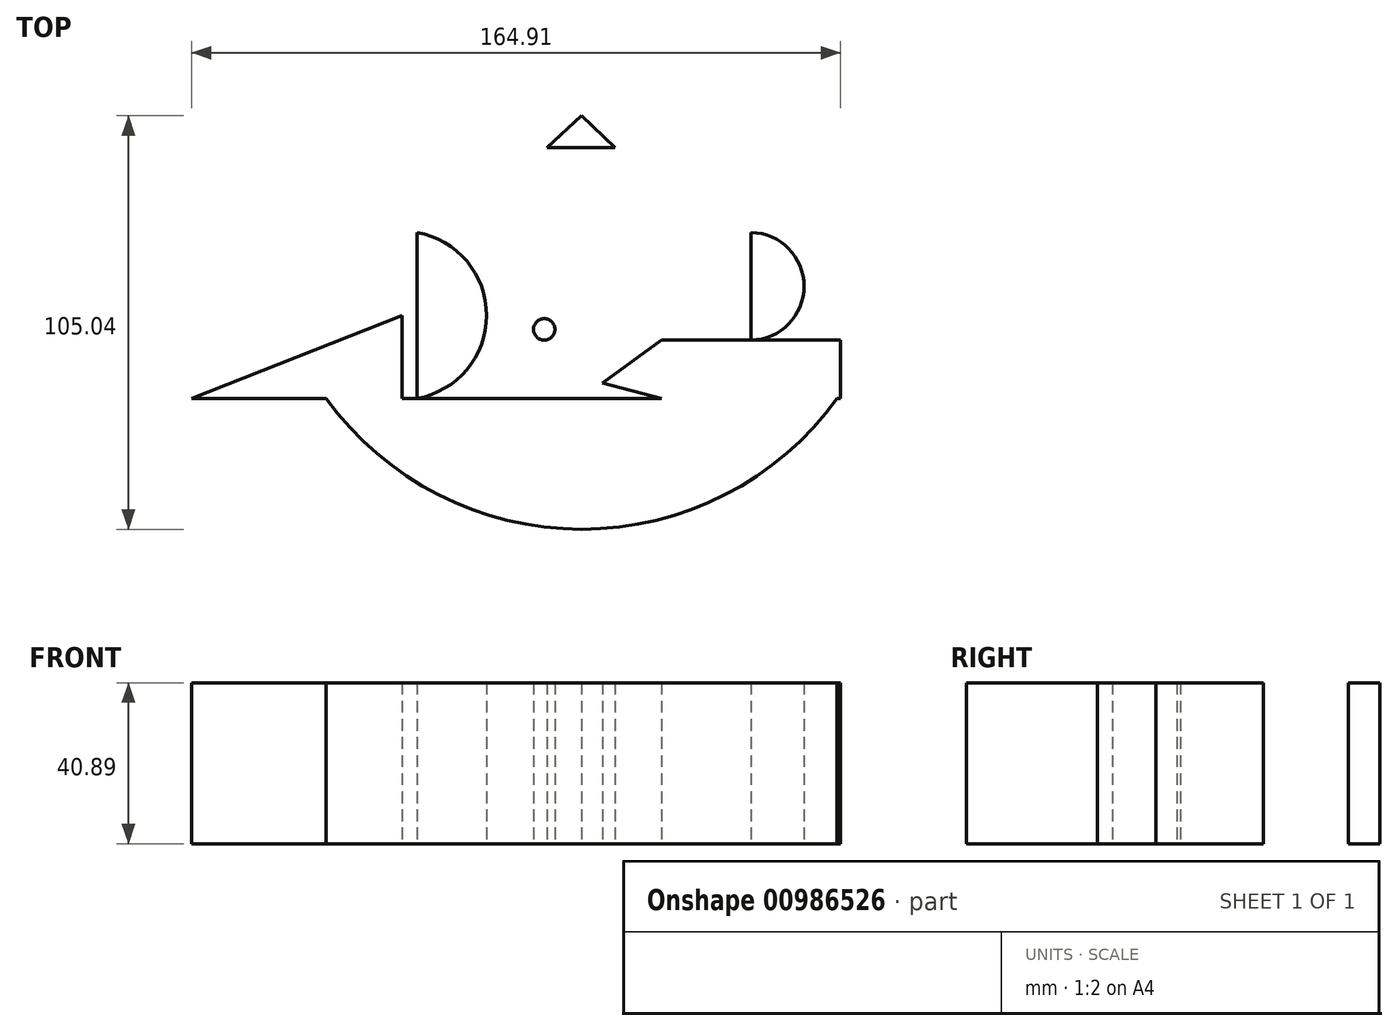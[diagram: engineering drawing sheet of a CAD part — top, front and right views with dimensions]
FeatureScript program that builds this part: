
annotation { "Feature Type Name" : "Feature", "Feature Type Description" : "" }
export const myFeature = defineFeature(function(context is Context, id is Id, definition is map)
    precondition{}
    {
        {
            var Q0;
            Q0=qCreatedBy(makeId("Top.planeOp"),FACE);
            var sketch = newSketch(context, id + "F0", { "sketchPlane" : qUnion([Q0])});
            skLineSegment(sketch, "E0", {"start": v(-64.9, 0) * mm, "end": v(64.9, 0) * mm});
            skArc(sketch, "E1", {"start": v(-64.9, 0) * mm, "mid": v(0, -33.23) * mm, "end": v(64.9, 0) * mm});
            skLineSegment(sketch, "E2.bottom", {"start": v(0, 0) * mm, "end": v(64.04, 0) * mm});
            skLineSegment(sketch, "E3.bottom", {"start": v(0, 0) * mm, "end": v(64.61, 0) * mm});
            skLineSegment(sketch, "E4.bottom", {"start": v(20.3, 0) * mm, "end": v(65.76, 0) * mm});
            skLineSegment(sketch, "E4.top", {"start": v(20.3, 14.82) * mm, "end": v(65.76, 14.82) * mm});
            skLineSegment(sketch, "E4.left", {"start": v(20.3, 0) * mm, "end": v(20.3, 14.82) * mm});
            skLineSegment(sketch, "E4.right", {"start": v(65.76, 0) * mm, "end": v(65.76, 14.82) * mm});
            skLineSegment(sketch, "E5", {"start": v(0, 0) * mm, "end": v(0, 63.75) * mm});
            skLineSegment(sketch, "E6", {"start": v(-41.88, 0) * mm, "end": v(-41.88, 42.16) * mm});
            skLineSegment(sketch, "E7", {"start": v(-8.78, 63.75) * mm, "end": v(8.5, 63.75) * mm});
            skArc(sketch, "E8", {"start": v(-41.88, 0) * mm, "mid": v(-24.17, 21.08) * mm, "end": v(-41.88, 42.16) * mm});
            skArc(sketch, "E9", {"start": v(43.03, 14.82) * mm, "mid": v(56.49, 28.5) * mm, "end": v(43.03, 42.16) * mm});
            skLineSegment(sketch, "E10", {"start": v(-8.78, 63.75) * mm, "end": v(0, 71.8) * mm});
            skLineSegment(sketch, "E11", {"start": v(8.5, 63.75) * mm, "end": v(0, 71.8) * mm});
            skLineSegment(sketch, "E12", {"start": v(43.03, 42.16) * mm, "end": v(43.03, 14.82) * mm});
            skLineSegment(sketch, "E13", {"start": v(20.3, 14.82) * mm, "end": v(0, 0) * mm});
            skLineSegment(sketch, "E14", {"start": v(20.3, 0) * mm, "end": v(16.07, 11.74) * mm});
            skLineSegment(sketch, "E15", {"start": v(20.3, 0) * mm, "end": v(10.08, 7.36) * mm});
            skLineSegment(sketch, "E16", {"start": v(20.3, 0) * mm, "end": v(5.32, 3.89) * mm});
            skLineSegment(sketch, "E17", {"start": v(-64.9, 0) * mm, "end": v(-99.15, 0) * mm});
            skLineSegment(sketch, "E18", {"start": v(-45.58, 21.08) * mm, "end": v(-99.15, 0) * mm});
            skLineSegment(sketch, "E19", {"start": v(-45.58, 21.08) * mm, "end": v(-45.58, 0) * mm});
            skPoint(sketch, "E20.endSnap0", {"position": v(-41.88, 21.08) * mm});
            skCircle(sketch, "E21", {"center": v(-9.52, 17.54) * mm, "radius": 2.75 * mm});
            skCircle(sketch, "E22", {"center": v(-9.52, 17.54) * mm, "radius": 2.72 * mm});
            skLineSegment(sketch, "E23", {"start": v(-11.06, 15.26) * mm, "end": v(-11.06, 0) * mm});
            skPoint(sketch, "E24.startSnap0", {"position": v(-11.06, 7.63) * mm});
            skLineSegment(sketch, "E25", {"start": v(-9.35, 20.87) * mm, "end": v(-9.35, 26.62) * mm});
            skLineSegment(sketch, "E26", {"start": v(-12.24, 17.54) * mm, "end": v(-18.28, 17.54) * mm});
            skLineSegment(sketch, "E27", {"start": v(-6.76, 17.54) * mm, "end": v(0, 19.97) * mm});
            skLineSegment(sketch, "E28", {"start": v(-7.71, 15.5) * mm, "end": v(-4.46, 11.37) * mm});
            skSolve(sketch);
        }
        {
            var Q0;
            {var subQ5=sQuery(id+"F0.wireOp",EDGE,"E1");Q0=makeQuery(id+"F0.imprint","IMPRINT",FACE,{"disambiguationData":[TD([[makeQuery(id+"F0.imprint","IMPRINT",EDGE,{"derivedFrom":subQ5}),1.0]])]});}
            var Q1;
            {var subQ5=sQuery(id+"F0.wireOp",EDGE,"E4.left");Q1=makeQuery(id+"F0.imprint","IMPRINT",FACE,{"disambiguationData":[TD([[makeQuery(id+"F0.imprint","IMPRINT",EDGE,{"derivedFrom":subQ5}),-1.0]])]});}
            var Q2;
            {var subQ0=sQuery(id+"F0.wireOp",EDGE,"E17");Q2=makeQuery(id+"F0.imprint","IMPRINT",FACE,{"disambiguationData":[TD([[makeQuery(id+"F0.imprint","IMPRINT",EDGE,{"derivedFrom":subQ0}),-1.0]])]});}
            var Q3;
            Q3=makeQuery(id+"F0.imprint","IMPRINT",FACE,{"disambiguationData":[TD([[makeQuery(id+"F0.imprint","IMPRINT",EDGE,{"derivedFrom":sQuery(id+"F0.wireOp",EDGE,"E6")}),-1.0]])]});
            var Q4;
            {var subQ2=sQuery(id+"F0.wireOp",EDGE,"E10");Q4=makeQuery(id+"F0.imprint","IMPRINT",FACE,{"disambiguationData":[TD([[makeQuery(id+"F0.imprint","IMPRINT",EDGE,{"derivedFrom":subQ2}),-1.0]])]});}
            var Q5;
            {var subQ0=sQuery(id+"F0.wireOp",EDGE,"E15");Q5=makeQuery(id+"F0.imprint","IMPRINT",FACE,{"disambiguationData":[TD([[makeQuery(id+"F0.imprint","IMPRINT",EDGE,{"derivedFrom":subQ0}),1.0]])]});}
            var Q6;
            {var subQ0=sQuery(id+"F0.wireOp",EDGE,"E3.bottom");Q6=makeQuery(id+"F0.imprint","IMPRINT",FACE,{"disambiguationData":[TD([[makeQuery(id+"F0.imprint","IMPRINT",EDGE,{"derivedFrom":subQ0}),1.0]])]});}
            var Q7;
            {var subQ0=sQuery(id+"F0.wireOp",EDGE,"E4.left");Q7=makeQuery(id+"F0.imprint","IMPRINT",FACE,{"disambiguationData":[TD([[makeQuery(id+"F0.imprint","IMPRINT",EDGE,{"derivedFrom":subQ0}),1.0]])]});}
            var Q8;
            {var subQ0=sQuery(id+"F0.wireOp",EDGE,"E14");Q8=makeQuery(id+"F0.imprint","IMPRINT",FACE,{"disambiguationData":[TD([[makeQuery(id+"F0.imprint","IMPRINT",EDGE,{"derivedFrom":subQ0}),1.0]])]});}
            var Q9;
            Q9=makeQuery(id+"F0.imprint","IMPRINT",FACE,{"disambiguationData":[TD([[makeQuery(id+"F0.imprint","IMPRINT",EDGE,{"derivedFrom":sQuery(id+"F0.wireOp",EDGE,"E9")}),1.0]])]});
            var Q10;
            {var subQ0=sQuery(id+"F0.wireOp",EDGE,"E22");var subQ1=makeQuery(id+"F0.imprint","INTERSECT",VERTEX,{"derivedFrom":[subQ0,sQuery(id+"F0.wireOp",EDGE,"E26")]});Q10=makeQuery(id+"F0.imprint","IMPRINT",FACE,{"disambiguationData":[TD([[makeQuery(id+"F0.imprint","IMPRINT",EDGE,{"disambiguationData":[TD([[subQ1,-1.0]])],"derivedFrom":subQ0}),1.0]])]});}
            extrude(context, id + "F1", {"entities" : qUnion([Q0, Q1, Q2, Q3, Q4, Q5, Q6, Q7, Q8, Q9, Q10]), "depth" : 40.9 * mm, "offsetDistance" : 25.4 * mm});
        }
    });
